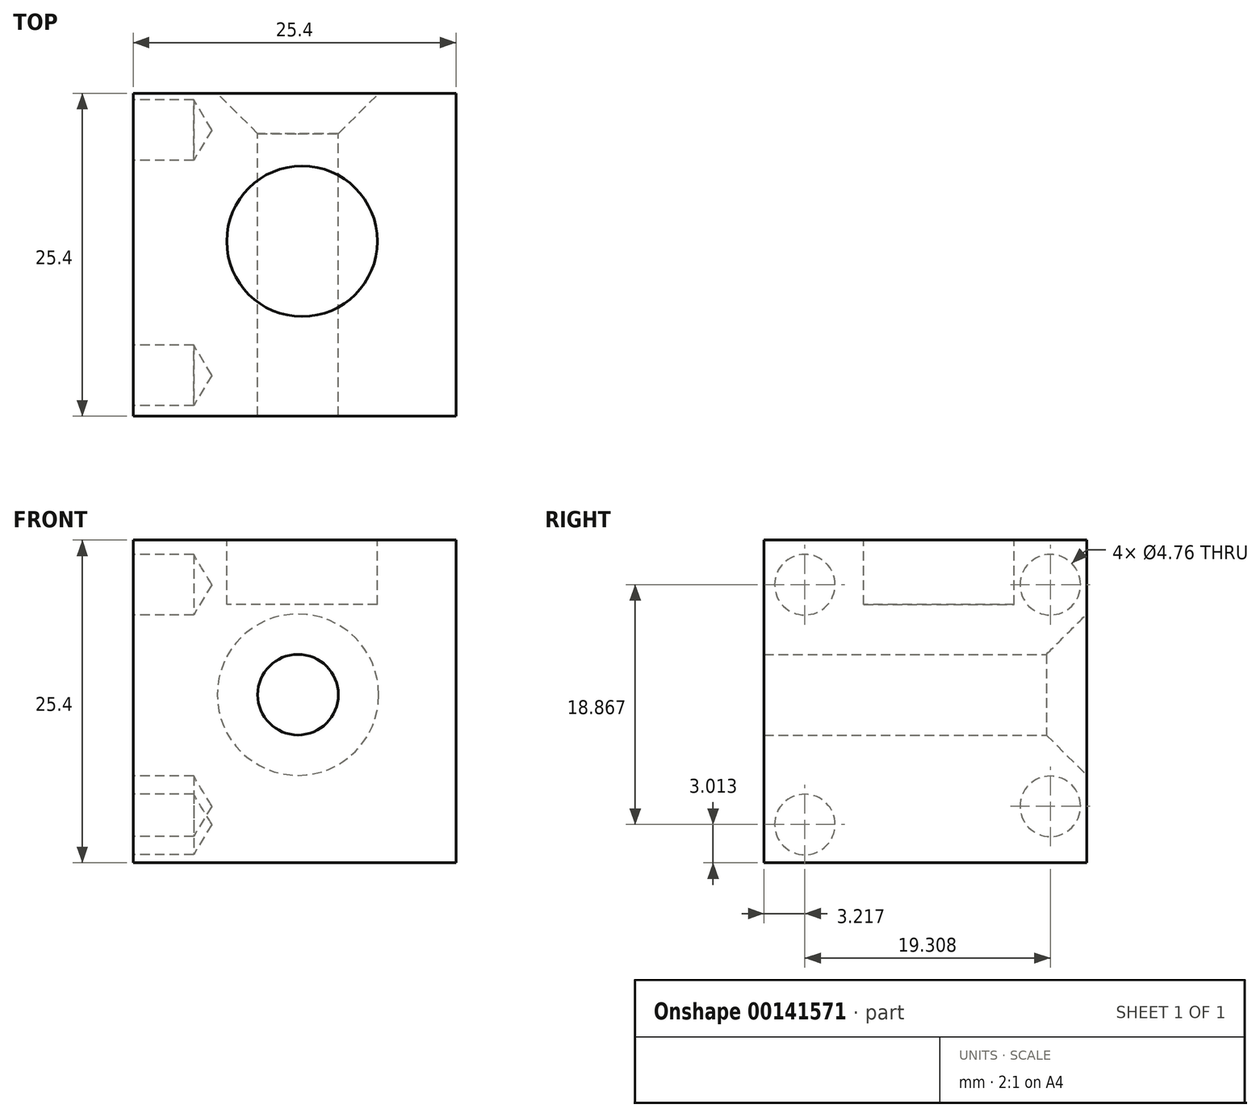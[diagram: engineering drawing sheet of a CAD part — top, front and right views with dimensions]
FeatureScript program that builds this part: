
annotation { "Feature Type Name" : "Feature", "Feature Type Description" : "" }
export const myFeature = defineFeature(function(context is Context, id is Id, definition is map)
    precondition{}
    {
        {
            var Q0;
            Q0=qCreatedBy(makeId("Front.planeOp"),FACE);
            var sketch = newSketch(context, id + "F0", { "sketchPlane" : qUnion([Q0])});
            skLineSegment(sketch, "E0.bottom", {"start": v(0, 0) * mm, "end": v(25.4, 0) * mm});
            skLineSegment(sketch, "E0.top", {"start": v(0, 25.4) * mm, "end": v(25.4, 25.4) * mm});
            skLineSegment(sketch, "E0.left", {"start": v(0, 0) * mm, "end": v(0, 25.4) * mm});
            skLineSegment(sketch, "E0.right", {"start": v(25.4, 0) * mm, "end": v(25.4, 25.4) * mm});
            skSolve(sketch);
        }
        {
            var Q0;
            Q0=makeQuery(id+"F0.imprint","IMPRINT",FACE,{"disambiguationData":[TD([[makeQuery(id+"F0.imprint","IMPRINT",EDGE,{"derivedFrom":sQuery(id+"F0.wireOp",EDGE,"E0.bottom")}),1.0]])]});
            extrude(context, id + "F1", {"entities" : qUnion([Q0]), "depth" : 25.4 * mm});
        }
        {
            var Q0;
            Q0=makeQuery(id+"F1.opExtrude","SWEPT_FACE",FACE,{"disambiguationData":[OSD([sQuery(id+"F0.wireOp",EDGE,"E0.left")])]});
            var sketch = newSketch(context, id + "F2", { "sketchPlane" : qUnion([Q0])});
            skPoint(sketch, "E1", {"position": v(2.87, 21.88) * mm});
            skPoint(sketch, "E2", {"position": v(2.87, 4.44) * mm});
            skPoint(sketch, "E3", {"position": v(22.18, 21.88) * mm});
            skPoint(sketch, "E4", {"position": v(22.18, 3.01) * mm});
            skSolve(sketch);
        }
        {
            var Q0;
            Q0=sQuery(id+"F2.wireOp",VERTEX,"E1");
            var Q1;
            Q1=sQuery(id+"F2.wireOp",VERTEX,"E3");
            var Q2;
            Q2=sQuery(id+"F2.wireOp",VERTEX,"E4");
            var Q3;
            Q3=sQuery(id+"F2.wireOp",VERTEX,"E2");
            var Q4;
            Q4=makeQuery(id+"F1.opExtrude","SWEPT_BODY",BODY,{"disambiguationData":[OSD([sQuery(id+"F0.wireOp",EDGE,"E0.bottom"),sQuery(id+"F0.wireOp",EDGE,"E0.top"),sQuery(id+"F0.wireOp",EDGE,"E0.left"),sQuery(id+"F0.wireOp",EDGE,"E0.right")])]});
            hole(context, id + "F3", {"style" : HoleStyle.SIMPLE, "endStyle" : HoleEndStyle.BLIND, "holeDiameter" : 4.76 * mm, "holeDepth" : 4.76 * mm, "locations" : qUnion([Q0, Q1, Q2, Q3]), "scope" : qUnion([Q4])});
        }
        {
            var Q0;
            Q0=makeQuery(id+"F1.opExtrude","SWEPT_FACE",FACE,{"disambiguationData":[OSD([sQuery(id+"F0.wireOp",EDGE,"E0.top")])]});
            var sketch = newSketch(context, id + "F4", { "sketchPlane" : qUnion([Q0])});
            skCircle(sketch, "E5", {"center": v(13.3, -11.64) * mm, "radius": 5.93 * mm});
            skSolve(sketch);
        }
        {
            var Q0;
            Q0 = qSketchRegion(id + "F4", true);
            extrude(context, id + "F8", {"entities" : qUnion([Q0]), "operationType" : NewBodyOperationType.REMOVE, "oppositeDirection" : true, "depth" : 5.08 * mm});
        }
        {
            var Q0;
            Q0=makeQuery(id+"F1.opExtrude","CAP_FACE",FACE,{"disambiguationData":[OSD([sQuery(id+"F0.wireOp",EDGE,"E0.bottom"),sQuery(id+"F0.wireOp",EDGE,"E0.top"),sQuery(id+"F0.wireOp",EDGE,"E0.left"),sQuery(id+"F0.wireOp",EDGE,"E0.right")])],"isStart":true});
            var sketch = newSketch(context, id + "F5", { "sketchPlane" : qUnion([Q0])});
            skPoint(sketch, "E6", {"position": v(-12.98, 13.23) * mm});
            skSolve(sketch);
        }
        {
            var Q0;
            Q0=sQuery(id+"F5.wireOp",VERTEX,"E6");
            var Q1;
            Q1=makeQuery(id+"F1.opExtrude","SWEPT_BODY",BODY,{"disambiguationData":[OSD([sQuery(id+"F0.wireOp",EDGE,"E0.bottom"),sQuery(id+"F0.wireOp",EDGE,"E0.top"),sQuery(id+"F0.wireOp",EDGE,"E0.left"),sQuery(id+"F0.wireOp",EDGE,"E0.right")])]});
            hole(context, id + "F6", {"style" : HoleStyle.C_SINK, "endStyle" : HoleEndStyle.THROUGH, "holeDiameter" : 6.35 * mm, "cSinkDiameter" : 12.7 * mm, "cSinkAngle" : 90 * degree, "locations" : qUnion([Q0]), "scope" : qUnion([Q1]), "isTappedThrough" : true});
        }
    });
